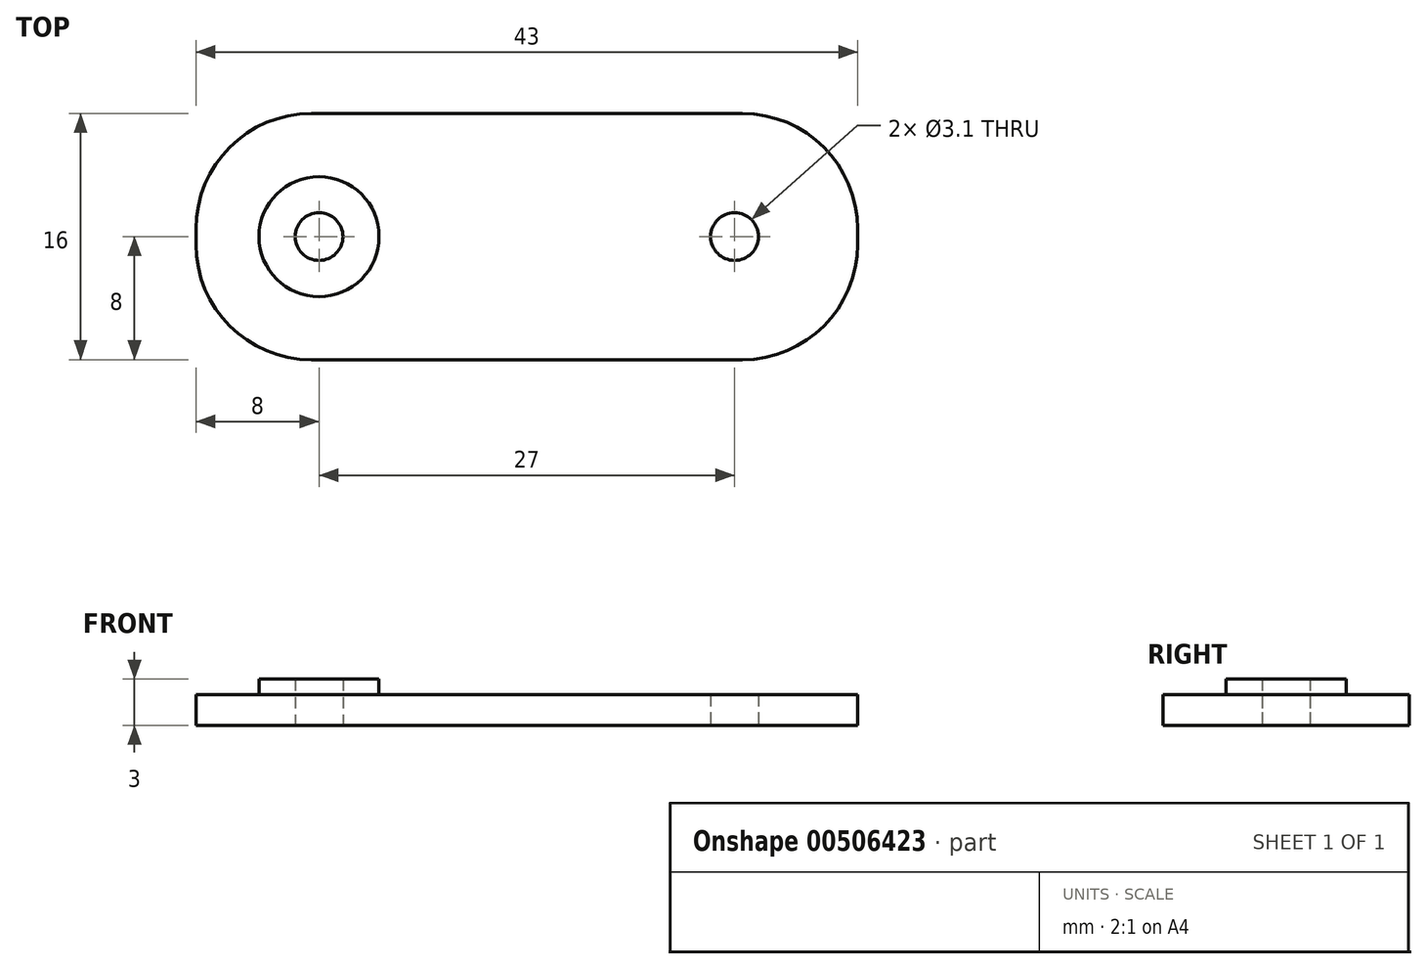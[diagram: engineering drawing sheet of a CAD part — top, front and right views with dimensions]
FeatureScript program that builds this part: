
annotation { "Feature Type Name" : "Feature", "Feature Type Description" : "" }
export const myFeature = defineFeature(function(context is Context, id is Id, definition is map)
    precondition{}
    {
        {
            var Q0;
            Q0=qCreatedBy(makeId("Top.planeOp"),FACE);
            var sketch = newSketch(context, id + "F0", { "sketchPlane" : qUnion([Q0])});
            skLineSegment(sketch, "E0.bottom", {"start": v(-21.5, 8) * mm, "end": v(21.5, 8) * mm});
            skLineSegment(sketch, "E0.top", {"start": v(-21.5, -8) * mm, "end": v(21.5, -8) * mm});
            skLineSegment(sketch, "E0.left", {"start": v(-21.5, 8) * mm, "end": v(-21.5, -8) * mm});
            skLineSegment(sketch, "E0.right", {"start": v(21.5, 8) * mm, "end": v(21.5, -8) * mm});
            skSolve(sketch);
        }
        {
            var Q0;
            Q0=makeQuery(id+"F0.imprint","IMPRINT",FACE,{"disambiguationData":[TD([[makeQuery(id+"F0.imprint","IMPRINT",EDGE,{"derivedFrom":sQuery(id+"F0.wireOp",EDGE,"E0.bottom")}),-1.0]])]});
            extrude(context, id + "F1", {"entities" : qUnion([Q0]), "depth" : 2 * mm});
        }
        {
            var Q0;
            Q0=qCreatedBy(makeId("Top.planeOp"),FACE);
            var sketch = newSketch(context, id + "F2", { "sketchPlane" : qUnion([Q0])});
            skCircle(sketch, "E1", {"center": v(-13.5, 0) * mm, "radius": 3.9 * mm});
            skCircle(sketch, "E2.MirrorC", {"center": v(13.5, 0) * mm, "radius": 3.9 * mm});
            skSolve(sketch);
        }
        {
            var Q0;
            Q0=makeQuery(id+"F2.imprint","IMPRINT",FACE,{"disambiguationData":[TD([[makeQuery(id+"F2.imprint","IMPRINT",EDGE,{"derivedFrom":sQuery(id+"F2.wireOp",EDGE,"E1")}),1.0]])]});
            var Q1;
            Q1=makeQuery(id+"F2.imprint","IMPRINT",FACE,{"disambiguationData":[TD([[makeQuery(id+"F2.imprint","IMPRINT",EDGE,{"derivedFrom":sQuery(id+"F2.wireOp",EDGE,"E2.MirrorC")}),-1.0]])]});
            extrude(context, id + "F3", {"entities" : qUnion([Q0, Q1]), "operationType" : NewBodyOperationType.ADD, "depth" : 3 * mm});
        }
        {
            var Q0;
            Q0=makeQuery(id+"F3.opExtrude","CAP_FACE",FACE,{"disambiguationData":[OSD([sQuery(id+"F2.wireOp",EDGE,"E1")])],"isStart":false});
            var sketch = newSketch(context, id + "F4", { "sketchPlane" : qUnion([Q0])});
            skPoint(sketch, "E3", {"position": v(-13.5, 0) * mm});
            skPoint(sketch, "E4.MirrorP", {"position": v(13.5, 0) * mm});
            skSolve(sketch);
        }
        {
            var Q0;
            Q0=sQuery(id+"F4.wireOp",VERTEX,"E3");
            var Q1;
            Q1=sQuery(id+"F4.wireOp",VERTEX,"E4.MirrorP");
            var Q2;
            Q2=makeQuery(id+"F1.opExtrude","SWEPT_BODY",BODY,{"disambiguationData":[OSD([sQuery(id+"F0.wireOp",EDGE,"E0.bottom"),sQuery(id+"F0.wireOp",EDGE,"E0.top"),sQuery(id+"F0.wireOp",EDGE,"E0.left"),sQuery(id+"F0.wireOp",EDGE,"E0.right")])]});
            hole(context, id + "F5", {"style" : HoleStyle.SIMPLE, "endStyle" : HoleEndStyle.THROUGH, "holeDiameter" : 3.1 * mm, "isTappedThrough" : true, "tappedDepth" : 12 * mm, "tapClearance" : 3, "startFromSketch" : true, "locations" : qUnion([Q0, Q1]), "scope" : qUnion([Q2])});
        }
        {
            var Q0;
            Q0=makeQuery(id+"F1.opExtrude","SWEPT_EDGE",EDGE,{"disambiguationData":[OSD([sQuery(id+"F0.wireOp",EDGE,"E0.top"),sQuery(id+"F0.wireOp",EDGE,"E0.left")])]});
            var Q1;
            Q1=makeQuery(id+"F1.opExtrude","SWEPT_EDGE",EDGE,{"disambiguationData":[OSD([sQuery(id+"F0.wireOp",EDGE,"E0.top"),sQuery(id+"F0.wireOp",EDGE,"E0.right")])]});
            var Q2;
            Q2=makeQuery(id+"F1.opExtrude","SWEPT_EDGE",EDGE,{"disambiguationData":[OSD([sQuery(id+"F0.wireOp",EDGE,"E0.bottom"),sQuery(id+"F0.wireOp",EDGE,"E0.right")])]});
            var Q3;
            Q3=makeQuery(id+"F1.opExtrude","SWEPT_EDGE",EDGE,{"disambiguationData":[OSD([sQuery(id+"F0.wireOp",EDGE,"E0.bottom"),sQuery(id+"F0.wireOp",EDGE,"E0.left")])]});
            fillet(context, id + "F6", {"entities" : qUnion([Q0, Q1, Q2, Q3]), "radius" : 7.5 * mm, "tangentPropagation" : true, "allowEdgeOverflow" : false});
        }
    });
